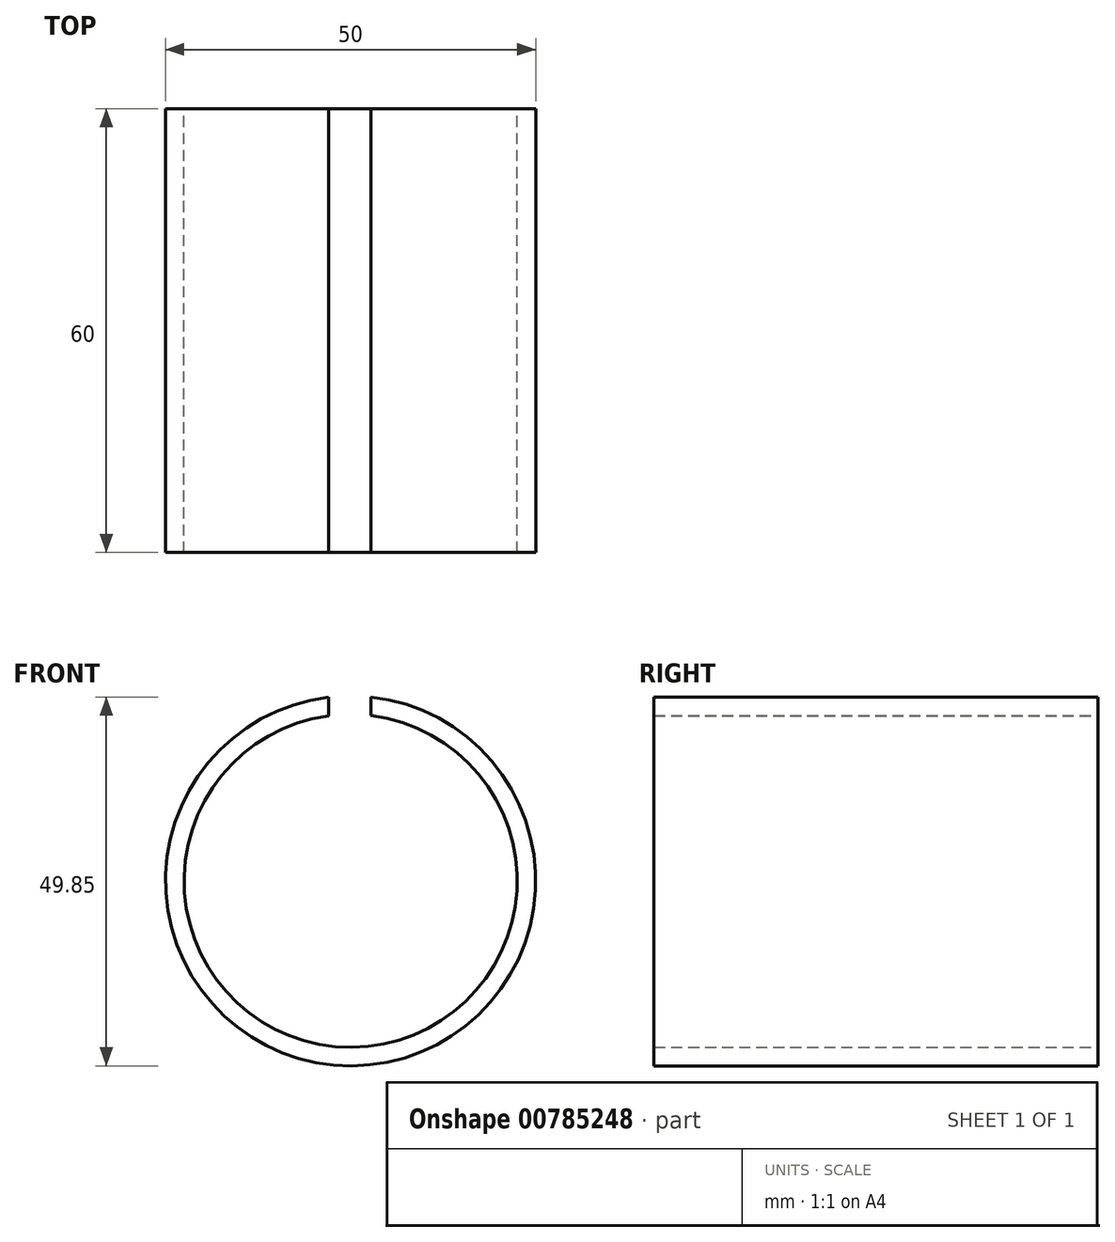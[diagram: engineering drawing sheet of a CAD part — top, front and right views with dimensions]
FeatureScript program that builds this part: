
annotation { "Feature Type Name" : "Feature", "Feature Type Description" : "" }
export const myFeature = defineFeature(function(context is Context, id is Id, definition is map)
    precondition{}
    {
        {
            var Q0;
            Q0=qCreatedBy(makeId("Front.planeOp"),FACE);
            var sketch = newSketch(context, id + "F0", { "sketchPlane" : qUnion([Q0])});
            skCircle(sketch, "E0", {"center": v(0, 0) * mm, "radius": 22.5 * mm});
            skCircle(sketch, "E1", {"center": v(0, 0) * mm, "radius": 25 * mm});
            skLineSegment(sketch, "E2", {"start": v(0, 0) * mm, "end": v(-3, 0) * mm});
            skLineSegment(sketch, "E3", {"start": v(0, 0) * mm, "end": v(2.74, 0) * mm});
            skLineSegment(sketch, "E4", {"start": v(2.74, 0) * mm, "end": v(2.74, 27.69) * mm});
            skLineSegment(sketch, "E5", {"start": v(2.74, 27.69) * mm, "end": v(-3, 27.69) * mm});
            skLineSegment(sketch, "E6", {"start": v(-3, 27.69) * mm, "end": v(-3, 0) * mm});
            skSolve(sketch);
        }
        {
            var Q0;
            {var subQ0=sQuery(id+"F0.wireOp",EDGE,"E4");var subQ1=sQuery(id+"F0.wireOp",EDGE,"E0");var subQ2=makeQuery(id+"F0.imprint","INTERSECT",VERTEX,{"derivedFrom":[subQ1,subQ0]});Q0=makeQuery(id+"F0.imprint","IMPRINT",FACE,{"disambiguationData":[TD([[makeQuery(id+"F0.imprint","IMPRINT",EDGE,{"disambiguationData":[TD([[subQ2,1.0]])],"derivedFrom":subQ1}),-1.0]])]});}
            extrude(context, id + "F1", {"entities" : qUnion([Q0]), "depth" : 60 * mm, "offsetDistance" : 25 * mm});
        }
    });
